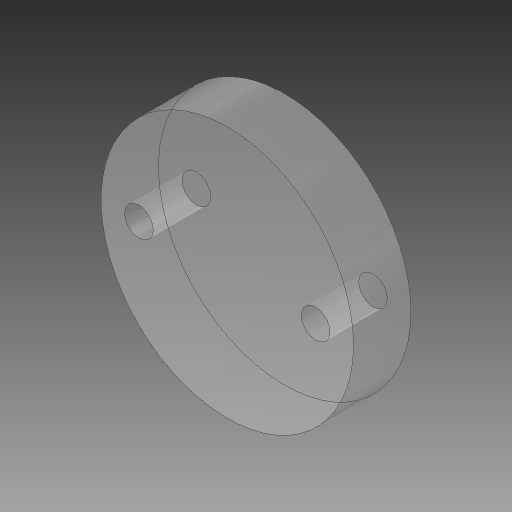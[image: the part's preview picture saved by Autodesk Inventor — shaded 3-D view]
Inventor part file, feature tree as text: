
AUTODESK INVENTOR PART (.ipt)
format: ipt  version: 2019.4 (Build 234330000, 330)  size: 111,104 bytes
history: native  units: mm
features: extrude x1, sketch x1
ambient origin geometry x8: Origin, YZ Plane, XZ Plane, XY Plane, X Axis, Y Axis, Z Axis, Center Point
bodies: Solid1 (feature_tree)
feature tree (2):
  extrude  "Extrusion1"  Depth=5.0mm
  sketch  "Sketch1"  dims[d0=22.0mm d1=15.4mm d2=2.5mm d3=2.5mm d4=5.0mm d5=0.0mm]
